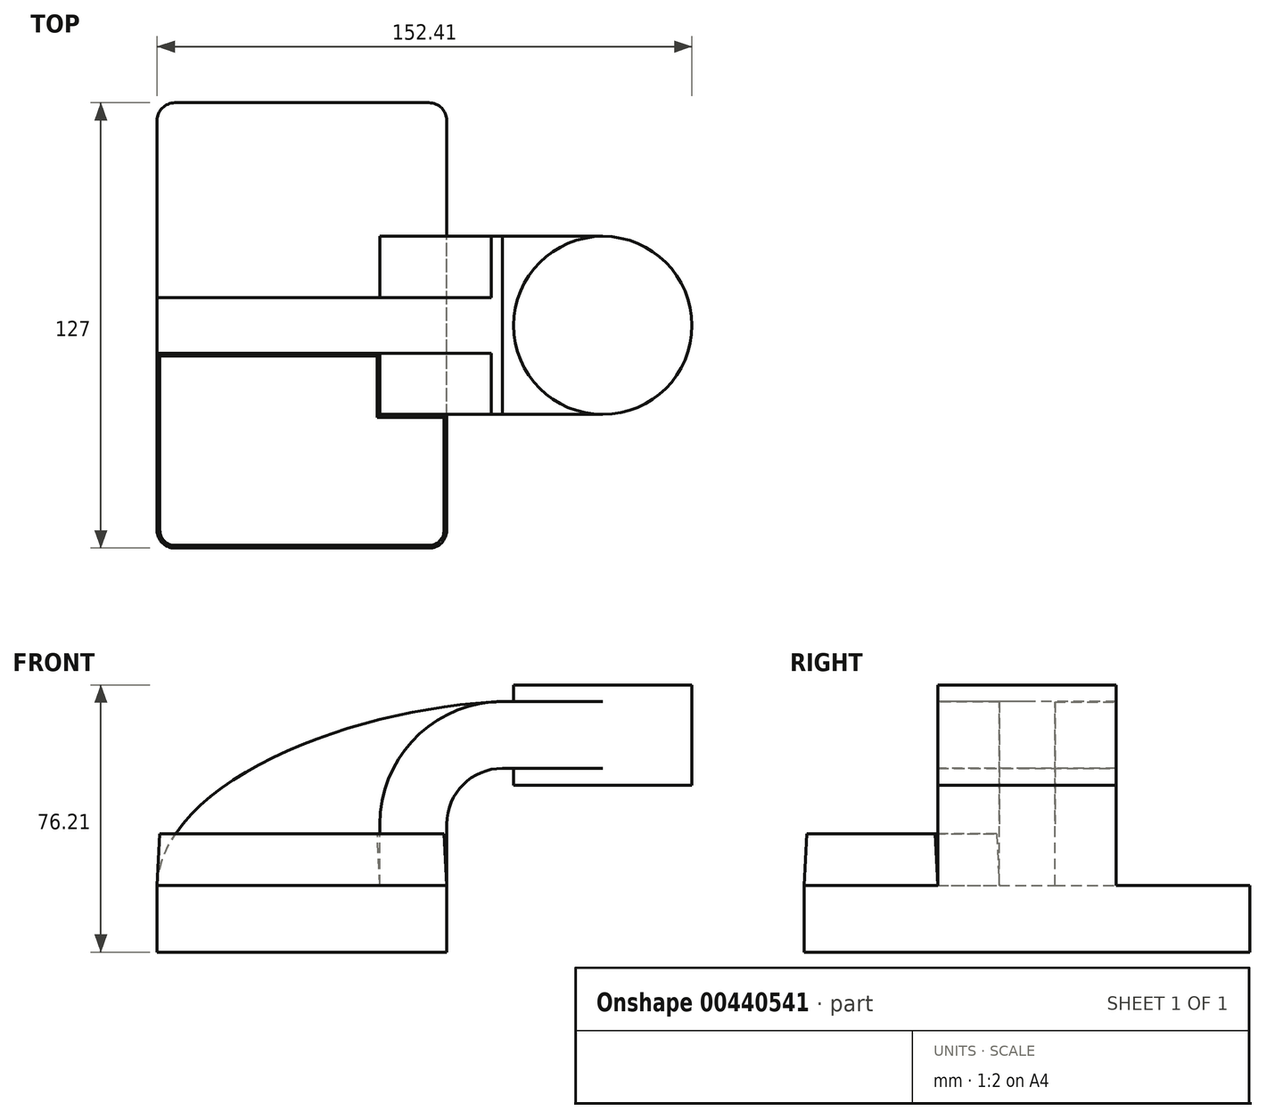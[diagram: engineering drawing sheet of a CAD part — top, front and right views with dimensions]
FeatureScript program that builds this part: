
annotation { "Feature Type Name" : "Feature", "Feature Type Description" : "" }
export const myFeature = defineFeature(function(context is Context, id is Id, definition is map)
    precondition{}
    {
        {
            var Q0;
            Q0=qCreatedBy(makeId("Front.planeOp"),FACE);
            var sketch = newSketch(context, id + "F0", { "sketchPlane" : qUnion([Q0])});
            skLineSegment(sketch, "E0.rect.bottom", {"start": v(-41.28, 9.52) * mm, "end": v(41.28, 9.52) * mm});
            skLineSegment(sketch, "E0.rect.top", {"start": v(-41.28, -9.52) * mm, "end": v(41.28, -9.52) * mm});
            skLineSegment(sketch, "E0.rect.left", {"start": v(-41.28, 9.52) * mm, "end": v(-41.28, -9.52) * mm});
            skLineSegment(sketch, "E0.rect.right", {"start": v(41.28, 9.52) * mm, "end": v(41.28, -9.52) * mm});
            skPoint(sketch, "E0.rect.middle", {"position": v(0, 0) * mm});
            skLineSegment(sketch, "E1", {"start": v(41.28, 9.52) * mm, "end": v(41.28, 27) * mm});
            skArc(sketch, "E2", {"start": v(41.28, 27) * mm, "mid": v(45.92, 38.23) * mm, "end": v(57.15, 42.88) * mm});
            skLineSegment(sketch, "E3", {"start": v(57.15, 42.88) * mm, "end": v(85.72, 42.88) * mm});
            skLineSegment(sketch, "E4.rect.bottom", {"start": v(60.32, 38.1) * mm, "end": v(111.12, 38.1) * mm});
            skLineSegment(sketch, "E4.rect.top", {"start": v(60.32, 66.68) * mm, "end": v(111.12, 66.68) * mm});
            skLineSegment(sketch, "E4.rect.left", {"start": v(60.32, 38.1) * mm, "end": v(60.32, 66.68) * mm});
            skLineSegment(sketch, "E4.rect.right", {"start": v(111.13, 38.1) * mm, "end": v(111.12, 66.68) * mm});
            skPoint(sketch, "E4.rect.middle", {"position": v(85.72, 52.39) * mm});
            skLineSegment(sketch, "E5.0", {"start": v(57.15, 61.93) * mm, "end": v(85.72, 61.93) * mm});
            skArc(sketch, "E5.1", {"start": v(22.23, 27) * mm, "mid": v(32.45, 51.7) * mm, "end": v(57.15, 61.93) * mm});
            skLineSegment(sketch, "E5.2", {"start": v(22.23, 9.52) * mm, "end": v(22.23, 27) * mm});
            skLineSegment(sketch, "E6", {"start": v(85.72, 38.1) * mm, "end": v(85.72, 66.68) * mm});
            skFitSpline(sketch, "E7", {"points": [v(-41.28, 9.53) * mm, v(57.15, 61.93) * mm], "startDerivative": vector(5.2, 92.34) * mm, "endDerivative": vector(120.92, 4.22) * mm});
            skSolve(sketch);
        }
        {
            var Q0;
            Q0=makeQuery(id+"F0.imprint","IMPRINT",FACE,{"disambiguationData":[TD([[makeQuery(id+"F0.imprint","IMPRINT",EDGE,{"derivedFrom":sQuery(id+"F0.wireOp",EDGE,"E0.rect.top")}),1.0]])]});
            extrude(context, id + "F1", {"entities" : qUnion([Q0]), "endBound" : BoundingType.SYMMETRIC, "depth" : 127 * mm});
        }
        {
            var Q0;
            {var subQ9=sQuery(id+"F0.wireOp",EDGE,"E1");Q0=makeQuery(id+"F0.imprint","IMPRINT",FACE,{"disambiguationData":[TD([[makeQuery(id+"F0.imprint","IMPRINT",EDGE,{"derivedFrom":subQ9}),1.0]])]});}
            var Q1;
            {var subQ0=sQuery(id+"F0.wireOp",EDGE,"E6");var subQ1=sQuery(id+"F0.wireOp",EDGE,"E3");var subQ2=makeQuery(id+"F0.imprint","INTERSECT",VERTEX,{"derivedFrom":[subQ1,subQ0]});Q1=makeQuery(id+"F0.imprint","IMPRINT",FACE,{"disambiguationData":[TD([[makeQuery(id+"F0.imprint","IMPRINT",EDGE,{"disambiguationData":[TD([[subQ2,1.0]])],"derivedFrom":subQ1}),1.0]])]});}
            extrude(context, id + "F2", {"entities" : qUnion([Q0, Q1]), "operationType" : NewBodyOperationType.ADD, "endBound" : BoundingType.SYMMETRIC, "depth" : 50.8 * mm});
        }
        {
            var Q0;
            {var subQ3=sQuery(id+"F0.wireOp",EDGE,"E5.2");Q0=makeQuery(id+"F0.imprint","IMPRINT",FACE,{"disambiguationData":[TD([[makeQuery(id+"F0.imprint","IMPRINT",EDGE,{"derivedFrom":subQ3}),1.0]])]});}
            extrude(context, id + "F3", {"entities" : qUnion([Q0]), "operationType" : NewBodyOperationType.ADD, "endBound" : BoundingType.SYMMETRIC, "depth" : 15.88 * mm});
        }
        {
            var Q0;
            {var subQ5=sQuery(id+"F0.wireOp",EDGE,"E4.rect.right");Q0=makeQuery(id+"F0.imprint","IMPRINT",FACE,{"disambiguationData":[TD([[makeQuery(id+"F0.imprint","IMPRINT",EDGE,{"derivedFrom":subQ5}),1.0]])]});}
            var Q1;
            Q1=sQuery(id+"F0.wireOp",EDGE,"E6");
            revolve(context, id + "F4", {"operationType" : NewBodyOperationType.ADD, "entities" : qUnion([Q0]), "axis" : qUnion([Q1]), "revolveType" : RevolveType.FULL});
        }
        {
            var Q0;
            Q0=makeQuery(id+"F1.opExtrude","CAP_EDGE",EDGE,{"disambiguationData":[OSD([sQuery(id+"F0.wireOp",EDGE,"E0.rect.right")])],"isStart":false});
            var Q1;
            Q1=makeQuery(id+"F1.opExtrude","CAP_EDGE",EDGE,{"disambiguationData":[OSD([sQuery(id+"F0.wireOp",EDGE,"E0.rect.left")])],"isStart":false});
            var Q2;
            Q2=makeQuery(id+"F1.opExtrude","CAP_EDGE",EDGE,{"disambiguationData":[OSD([sQuery(id+"F0.wireOp",EDGE,"E0.rect.right")])],"isStart":true});
            var Q3;
            Q3=makeQuery(id+"F1.opExtrude","CAP_EDGE",EDGE,{"disambiguationData":[OSD([sQuery(id+"F0.wireOp",EDGE,"E0.rect.left")])],"isStart":true});
            fillet(context, id + "F5", {"entities" : qUnion([Q0, Q1, Q2, Q3]), "radius" : 5.08 * mm, "tangentPropagation" : true, "allowEdgeOverflow" : false});
        }
        {
            var Q0;
            {var subQ4=sQuery(id+"F0.wireOp",EDGE,"E0.rect.bottom");var subQ5=sQuery(id+"F0.wireOp",EDGE,"E0.rect.right");var subQ6=sQuery(id+"F0.wireOp",EDGE,"E0.rect.left");Q0=makeQuery(id+"F3.boolean.opBoolean","SPLIT",FACE,{"disambiguationData":[TD([makeQuery(id+"F1.opExtrude","CAP_FACE",FACE,{"disambiguationData":[OSD([subQ4,sQuery(id+"F0.wireOp",EDGE,"E0.rect.top"),subQ6,subQ5])],"isStart":false})])],"derivedFrom":makeQuery(id+"F1.opExtrude","SWEPT_FACE",FACE,{"disambiguationData":[OSD([subQ4])]})});}
            extrude(context, id + "F6", {"entities" : qUnion([Q0]), "operationType" : NewBodyOperationType.ADD, "depth" : 14.73 * mm, "hasDraft" : true, "draftAngle" : 3 * degree, "draftPullDirection" : true});
        }
    });
